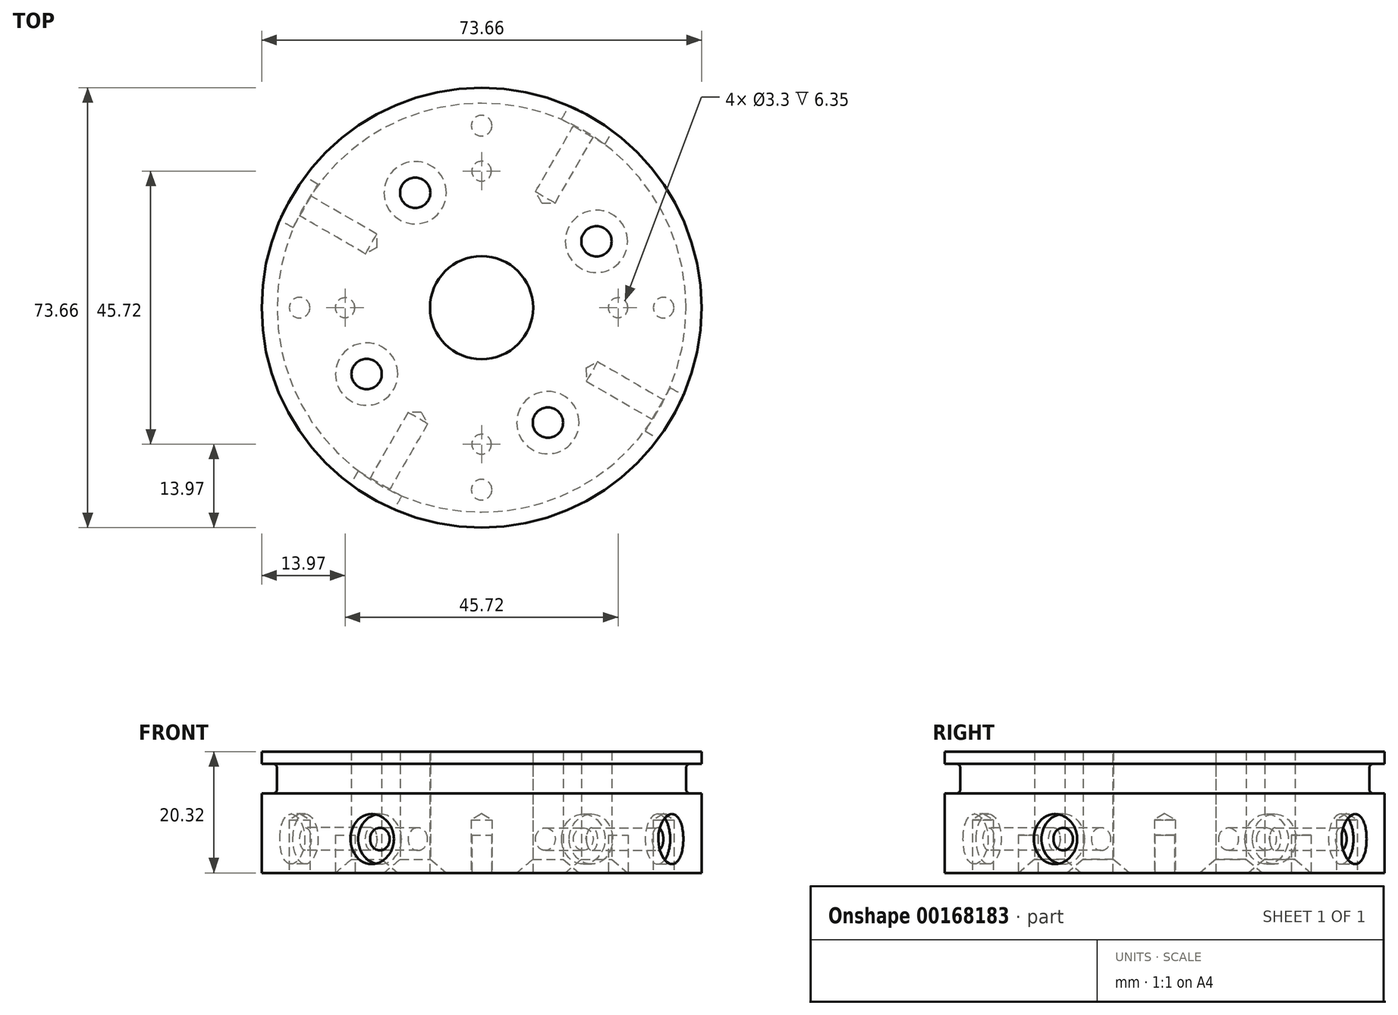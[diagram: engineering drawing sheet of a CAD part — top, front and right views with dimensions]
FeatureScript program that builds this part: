
annotation { "Feature Type Name" : "Feature", "Feature Type Description" : "" }
export const myFeature = defineFeature(function(context is Context, id is Id, definition is map)
    precondition{}
    {
        {
            var Q0;
            Q0=qCreatedBy(makeId("Top.planeOp"),FACE);
            var sketch = newSketch(context, id + "F0", { "sketchPlane" : qUnion([Q0])});
            skCircle(sketch, "E0", {"center": v(0, 0) * mm, "radius": 36.83 * mm});
            skSolve(sketch);
        }
        {
            var Q0;
            Q0=makeQuery(id+"F0.imprint","IMPRINT",FACE,{"disambiguationData":[TD([[makeQuery(id+"F0.imprint","IMPRINT",EDGE,{"derivedFrom":sQuery(id+"F0.wireOp",EDGE,"E0")}),1.0]])]});
            extrude(context, id + "F1", {"entities" : qUnion([Q0]), "depth" : 20.32 * mm});
        }
        {
            var Q0;
            Q0=makeQuery(id+"FNZgXB3MDCEPfWC_1.boolean.opBoolean","SPLIT",FACE,{"disambiguationData":[TD([makeQuery(id+"FNZgXB3MDCEPfWC_1.opExtrude","SWEPT_FACE",FACE,{"disambiguationData":[OSD([sQuery(id+"FiLk9hSRQ8Dv81E_1.wireOp",EDGE,"Xvq2NHEn-EDZK-GzOR-rNrk-moL4fFsD4KvI")])]})])],"derivedFrom":makeQuery(id+"F1.opExtrude","CAP_FACE",FACE,{"disambiguationData":[OSD([sQuery(id+"F0.wireOp",EDGE,"E0")])],"isStart":false})});
            var sketch = newSketch(context, id + "F2", { "sketchPlane" : qUnion([Q0])});
            skCircle(sketch, "E1", {"center": v(0, 0) * mm, "radius": 8.64 * mm});
            skSolve(sketch);
        }
        {
            var Q0;
            Q0=qSketchRegion(id+"F2",true);
            extrude(context, id + "F3", {"entities" : qUnion([Q0]), "operationType" : NewBodyOperationType.REMOVE, "endBound" : BoundingType.THROUGH_ALL, "oppositeDirection" : true, "depth" : 25.4 * mm});
        }
        {
            var Q0;
            Q0=makeQuery(id+"FOQC5dfjhO448EJ_1.boolean.opBoolean","SPLIT",FACE,{"disambiguationData":[TD([makeQuery(id+"F3.boolean.opBoolean","COPY",FACE,{"derivedFrom":makeQuery(id+"F3.opExtrude","SWEPT_FACE",FACE,{"disambiguationData":[OSD([sQuery(id+"F2.wireOp",EDGE,"E1")])]})})])],"derivedFrom":makeQuery(id+"F1.opExtrude","CAP_FACE",FACE,{"disambiguationData":[OSD([sQuery(id+"F0.wireOp",EDGE,"E0")])],"isStart":false})});
            cPlane(context, id + "F4", {"entities" : qUnion([Q0]), "cplaneType" : CPlaneType.OFFSET, "offset" : 2.03 * mm, "oppositeDirection" : true, "width" : 152.4 * mm, "height" : 152.4 * mm});
        }
        {
            var Q0;
            Q0=qCreatedBy(id+"F4.planeOp",FACE);
            var sketch = newSketch(context, id + "F5", { "sketchPlane" : qUnion([Q0])});
            skCircle(sketch, "E2", {"center": v(0, 0) * mm, "radius": 34.24 * mm});
            skCircle(sketch, "E3.0", {"center": v(0, 0) * mm, "radius": 36.83 * mm});
            skSolve(sketch);
        }
        {
            var Q0;
            Q0=qSketchRegion(id+"F5",true);
            extrude(context, id + "F6", {"entities" : qUnion([Q0]), "operationType" : NewBodyOperationType.REMOVE, "oppositeDirection" : true, "depth" : 5 * mm});
        }
        {
            var Q0;
            Q0=makeQuery(id+"F6.boolean.opBoolean","COPY",EDGE,{"derivedFrom":makeQuery(id+"F6.opExtrude","CAP_EDGE",EDGE,{"disambiguationData":[OSD([sQuery(id+"F5.wireOp",EDGE,"E2")])],"isStart":false})});
            var Q1;
            Q1=makeQuery(id+"F6.boolean.opBoolean","COPY",EDGE,{"derivedFrom":makeQuery(id+"F6.opExtrude","CAP_EDGE",EDGE,{"disambiguationData":[OSD([sQuery(id+"F5.wireOp",EDGE,"E2")])],"isStart":true})});
            fillet(context, id + "F7", {"entities" : qUnion([Q0, Q1]), "radius" : 0.76 * mm, "tangentPropagation" : true, "allowEdgeOverflow" : false});
        }
        {
            var Q0;
            {var subQ1=sQuery(id+"F0.wireOp",EDGE,"E0");var subQ2=makeQuery(id+"F1.opExtrude","SWEPT_FACE",FACE,{"disambiguationData":[OSD([subQ1])]});Q0=makeQuery(id+"FkcieFRIapZdHPD_1.boolean.opBoolean","SPLIT",FACE,{"disambiguationData":[TD([subQ2])],"derivedFrom":makeQuery(id+"F1.opExtrude","CAP_FACE",FACE,{"disambiguationData":[OSD([subQ1])],"isStart":false})});}
            var sketch = newSketch(context, id + "F8", { "sketchPlane" : qUnion([Q0])});
            skCircle(sketch, "E4.0", {"center": v(0, 0) * mm, "radius": 36.83 * mm, "construction": true});
            skPoint(sketch, "E5", {"position": v(-18.41, -31.9) * mm});
            skLineSegment(sketch, "E6", {"start": v(0, -36.83) * mm, "end": v(0, 0) * mm, "construction": true});
            skLineSegment(sketch, "E7", {"start": v(0, 0) * mm, "end": v(-17.96, -31.1) * mm, "construction": true});
            skLineSegment(sketch, "E8", {"start": v(-17.96, -31.1) * mm, "end": v(-18.41, -31.9) * mm, "construction": true});
            skLineSegment(sketch, "E9", {"start": v(0, 0) * mm, "end": v(18.41, 31.9) * mm, "construction": true});
            skLineSegment(sketch, "E10", {"start": v(18.41, 31.9) * mm, "end": v(0, 0) * mm, "construction": true});
            skLineSegment(sketch, "E11", {"start": v(31.9, -18.41) * mm, "end": v(0, 0) * mm, "construction": true});
            skLineSegment(sketch, "E12", {"start": v(0, 0) * mm, "end": v(-31.9, 18.41) * mm, "construction": true});
            skPoint(sketch, "E13", {"position": v(18.41, 31.9) * mm});
            skPoint(sketch, "E14", {"position": v(31.9, -18.41) * mm});
            skPoint(sketch, "E15", {"position": v(-31.9, 18.41) * mm});
            skSolve(sketch);
        }
        {
            var Q0;
            Q0=qCreatedBy(makeId("Front.planeOp"),FACE);
            var sketch = newSketch(context, id + "F9", { "sketchPlane" : qUnion([Q0])});
            skLineSegment(sketch, "E16", {"start": v(0, 0) * mm, "end": v(0, 38.57) * mm, "construction": true});
            skSolve(sketch);
        }
        {
            var Q0;
            Q0=sQuery(id+"F9.wireOp",EDGE,"E16");
            cPlane(context, id + "F10", {"entities" : qUnion([Q0]), "cplaneType" : CPlaneType.LINE_ANGLE, "offset" : 25.4 * mm, "angle" : 60 * degree, "width" : 152.4 * mm, "height" : 152.4 * mm});
        }
        {
            var Q0;
            Q0=sQuery(id+"F8.wireOp",VERTEX,"E5");
            var Q1;
            Q1=qCreatedBy(id+"F10.planeOp",FACE);
            cPlane(context, id + "F11", {"entities" : qUnion([Q0, Q1]), "cplaneType" : CPlaneType.PLANE_POINT, "offset" : 25.4 * mm, "width" : 152.4 * mm, "height" : 152.4 * mm});
        }
        {
            var Q0;
            Q0=qCreatedBy(id+"F11.planeOp",FACE);
            var Q1;
            Q1=sQuery(id+"F8.wireOp",VERTEX,"E13");
            cPlane(context, id + "F12", {"entities" : qUnion([Q0, Q1]), "cplaneType" : CPlaneType.PLANE_POINT, "offset" : 25.4 * mm, "width" : 152.4 * mm, "height" : 152.4 * mm});
        }
        {
            var Q0;
            Q0=sQuery(id+"F9.wireOp",EDGE,"E16");
            cPlane(context, id + "F13", {"entities" : qUnion([Q0]), "cplaneType" : CPlaneType.LINE_ANGLE, "offset" : 25.4 * mm, "angle" : 150 * degree, "width" : 152.4 * mm, "height" : 152.4 * mm});
        }
        {
            var Q0;
            Q0=sQuery(id+"F8.wireOp",VERTEX,"E15");
            var Q1;
            Q1=qCreatedBy(id+"F13.planeOp",FACE);
            cPlane(context, id + "F14", {"entities" : qUnion([Q0, Q1]), "cplaneType" : CPlaneType.PLANE_POINT, "offset" : 25.4 * mm, "width" : 152.4 * mm, "height" : 152.4 * mm});
        }
        {
            var Q0;
            Q0=qCreatedBy(id+"F13.planeOp",FACE);
            var Q1;
            Q1=sQuery(id+"F8.wireOp",VERTEX,"E14");
            cPlane(context, id + "F15", {"entities" : qUnion([Q0, Q1]), "cplaneType" : CPlaneType.PLANE_POINT, "offset" : 25.4 * mm, "width" : 152.4 * mm, "height" : 152.4 * mm});
        }
        {
            var Q0;
            Q0=qCreatedBy(id+"F11.planeOp",FACE);
            var sketch = newSketch(context, id + "F16", { "sketchPlane" : qUnion([Q0])});
            skLineSegment(sketch, "E17", {"start": v(0, 0) * mm, "end": v(0, 5.66) * mm, "construction": true});
            skPoint(sketch, "E18", {"position": v(0, 5.66) * mm});
            skSolve(sketch);
        }
        {
            var Q0;
            Q0=qCreatedBy(id+"F12.planeOp",FACE);
            var sketch = newSketch(context, id + "F17", { "sketchPlane" : qUnion([Q0])});
            skPoint(sketch, "E19", {"position": v(0, 5.66) * mm});
            skLineSegment(sketch, "E20.0", {"start": v(0, 0) * mm, "end": v(0, 5.66) * mm, "construction": true});
            skSolve(sketch);
        }
        {
            var Q0;
            Q0=qCreatedBy(id+"F14.planeOp",FACE);
            var sketch = newSketch(context, id + "F18", { "sketchPlane" : qUnion([Q0])});
            skLineSegment(sketch, "E21", {"start": v(0, 0) * mm, "end": v(0, 5.66) * mm, "construction": true});
            skLineSegment(sketch, "E22.0", {"start": v(-36.83, 0) * mm, "end": v(-36.83, 5.66) * mm, "construction": true});
            skPoint(sketch, "E23", {"position": v(0, 5.66) * mm});
            skLineSegment(sketch, "E24", {"start": v(-36.83, 5.66) * mm, "end": v(0, 5.66) * mm, "construction": true});
            skSolve(sketch);
        }
        {
            var Q0;
            Q0=qCreatedBy(id+"F15.planeOp",FACE);
            var sketch = newSketch(context, id + "F19", { "sketchPlane" : qUnion([Q0])});
            skLineSegment(sketch, "E25.0", {"start": v(0, 0) * mm, "end": v(0, 5.66) * mm, "construction": true});
            skPoint(sketch, "E26", {"position": v(0, 5.66) * mm});
            skSolve(sketch);
        }
        {
            var Q0;
            Q0=sQuery(id+"F19.wireOp",VERTEX,"E26");
            var Q1;
            Q1=makeQuery(id+"F1.opExtrude","SWEPT_BODY",BODY,{"disambiguationData":[OSD([sQuery(id+"F0.wireOp",EDGE,"E0")])]});
            hole(context, id + "F20", {"style" : HoleStyle.C_BORE, "endStyle" : HoleEndStyle.BLIND, "oppositeDirection" : true, "holeDiameter" : 3.8 * mm, "cBoreDiameter" : 8.38 * mm, "cBoreDepth" : 2.54 * mm, "holeDepth" : 15.24 * mm, "locations" : qUnion([Q0]), "scope" : qUnion([Q1])});
        }
        {
            var Q0;
            Q0=sQuery(id+"F18.wireOp",VERTEX,"E23");
            var Q1;
            Q1=makeQuery(id+"F1.opExtrude","SWEPT_BODY",BODY,{"disambiguationData":[OSD([sQuery(id+"F0.wireOp",EDGE,"E0")])]});
            hole(context, id + "F21", {"style" : HoleStyle.C_BORE, "endStyle" : HoleEndStyle.BLIND, "holeDiameter" : 3.8 * mm, "cBoreDiameter" : 8.38 * mm, "cBoreDepth" : 2.54 * mm, "holeDepth" : 15.24 * mm, "locations" : qUnion([Q0]), "scope" : qUnion([Q1])});
        }
        {
            var Q0;
            Q0=sQuery(id+"F16.wireOp",VERTEX,"E18");
            var Q1;
            Q1=makeQuery(id+"F1.opExtrude","SWEPT_BODY",BODY,{"disambiguationData":[OSD([sQuery(id+"F0.wireOp",EDGE,"E0")])]});
            hole(context, id + "F22", {"style" : HoleStyle.C_BORE, "endStyle" : HoleEndStyle.BLIND, "oppositeDirection" : true, "holeDiameter" : 3.8 * mm, "cBoreDiameter" : 8.38 * mm, "cBoreDepth" : 2.54 * mm, "holeDepth" : 15.24 * mm, "locations" : qUnion([Q0]), "scope" : qUnion([Q1])});
        }
        {
            var Q0;
            Q0=sQuery(id+"F17.wireOp",VERTEX,"E19");
            var Q1;
            Q1=makeQuery(id+"F1.opExtrude","SWEPT_BODY",BODY,{"disambiguationData":[OSD([sQuery(id+"F0.wireOp",EDGE,"E0")])]});
            hole(context, id + "F23", {"style" : HoleStyle.C_BORE, "endStyle" : HoleEndStyle.BLIND, "holeDiameter" : 3.8 * mm, "cBoreDiameter" : 8.38 * mm, "cBoreDepth" : 2.54 * mm, "holeDepth" : 15.24 * mm, "locations" : qUnion([Q0]), "scope" : qUnion([Q1])});
        }
        {
            var Q0;
            Q0=makeQuery(id+"F1.opExtrude","CAP_FACE",FACE,{"disambiguationData":[OSD([sQuery(id+"F0.wireOp",EDGE,"E0")])],"isStart":true});
            var sketch = newSketch(context, id + "F24", { "sketchPlane" : qUnion([Q0])});
            skLineSegment(sketch, "E27", {"start": v(0, 0) * mm, "end": v(-11.11, -19.25) * mm, "construction": true});
            skPoint(sketch, "E28", {"position": v(-11.11, -19.25) * mm});
            skPoint(sketch, "E29.1.0", {"position": v(19.25, -11.11) * mm});
            skPoint(sketch, "E29.2.0", {"position": v(11.11, 19.25) * mm});
            skPoint(sketch, "E29.3.0", {"position": v(-19.25, 11.11) * mm});
            skPoint(sketch, "E29.center", {"position": v(0, 0) * mm});
            skSolve(sketch);
        }
        {
            var Q0;
            Q0=sQuery(id+"F24.wireOp",VERTEX,"E29.3.0");
            var Q1;
            Q1=sQuery(id+"F24.wireOp",VERTEX,"E28");
            var Q2;
            Q2=sQuery(id+"F24.wireOp",VERTEX,"E29.1.0");
            var Q3;
            Q3=sQuery(id+"F24.wireOp",VERTEX,"E29.2.0");
            var Q4;
            Q4=makeQuery(id+"F1.opExtrude","SWEPT_BODY",BODY,{"disambiguationData":[OSD([sQuery(id+"F0.wireOp",EDGE,"E0")])]});
            hole(context, id + "F25", {"style" : HoleStyle.C_SINK, "endStyle" : HoleEndStyle.THROUGH, "holeDiameter" : 5.08 * mm, "cSinkDiameter" : 10.44 * mm, "cSinkAngle" : 100 * degree, "locations" : qUnion([Q0, Q1, Q2, Q3]), "scope" : qUnion([Q4]), "isTappedThrough" : true});
        }
        {
            var Q0;
            Q0=makeQuery(id+"F1.opExtrude","CAP_FACE",FACE,{"disambiguationData":[OSD([sQuery(id+"F0.wireOp",EDGE,"E0")])],"isStart":true});
            var sketch = newSketch(context, id + "F26", { "sketchPlane" : qUnion([Q0])});
            skPoint(sketch, "E30", {"position": v(-30.48, 0) * mm});
            skPoint(sketch, "E31.1.0", {"position": v(0, -30.48) * mm});
            skPoint(sketch, "E31.2.0", {"position": v(30.48, 0) * mm});
            skPoint(sketch, "E31.3.0", {"position": v(0, 30.48) * mm});
            skPoint(sketch, "E31.center", {"position": v(0, 0) * mm});
            skSolve(sketch);
        }
        {
            var Q0;
            Q0=sQuery(id+"F26.wireOp",VERTEX,"E30");
            var Q1;
            Q1=sQuery(id+"F26.wireOp",VERTEX,"E31.1.0");
            var Q2;
            Q2=sQuery(id+"F26.wireOp",VERTEX,"E31.3.0");
            var Q3;
            Q3=sQuery(id+"F26.wireOp",VERTEX,"E31.2.0");
            var Q4;
            Q4=makeQuery(id+"F1.opExtrude","SWEPT_BODY",BODY,{"disambiguationData":[OSD([sQuery(id+"F0.wireOp",EDGE,"E0")])]});
            hole(context, id + "F27", {"style" : HoleStyle.SIMPLE, "endStyle" : HoleEndStyle.BLIND, "standardTappedOrClearance" : lookupTablePath({ "standard" : "ANSI", "engagement" : "75%", "pitch" : "32 tpi", "size" : "#8", "type" : "Tapped" }), "standardBlindInLast" : lookupTablePath({ "standard" : "ANSI", "engagement" : "75%", "pitch" : "32 tpi", "size" : "#8", "type" : "Tapped" }), "holeDiameter" : 3.45 * mm, "holeDepth" : 8.9 * mm, "locations" : qUnion([Q0, Q1, Q2, Q3]), "scope" : qUnion([Q4]), "majorDiameter" : 4.17 * mm});
        }
        {
            var Q0;
            Q0=makeQuery(id+"F1.opExtrude","CAP_FACE",FACE,{"disambiguationData":[OSD([sQuery(id+"F0.wireOp",EDGE,"E0")])],"isStart":true});
            var sketch = newSketch(context, id + "F28", { "sketchPlane" : qUnion([Q0])});
            skCircle(sketch, "E32", {"center": v(-22.86, 0) * mm, "radius": 1.65 * mm});
            skCircle(sketch, "E33.1.0", {"center": v(0, -22.86) * mm, "radius": 1.65 * mm});
            skCircle(sketch, "E33.2.0", {"center": v(22.86, 0) * mm, "radius": 1.65 * mm});
            skCircle(sketch, "E33.3.0", {"center": v(0, 22.86) * mm, "radius": 1.65 * mm});
            skPoint(sketch, "E33.center", {"position": v(0, 0) * mm});
            skSolve(sketch);
        }
        {
            var Q0;
            Q0=qSketchRegion(id+"F28",true);
            extrude(context, id + "F29", {"entities" : qUnion([Q0]), "operationType" : NewBodyOperationType.REMOVE, "oppositeDirection" : true, "depth" : 6.35 * mm});
        }
    });
